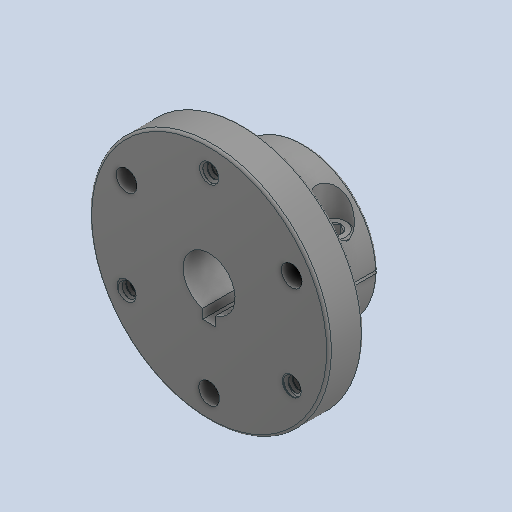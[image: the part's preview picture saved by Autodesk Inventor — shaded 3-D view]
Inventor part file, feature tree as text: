
AUTODESK INVENTOR PART (.ipt)
format: ipt  version: 2022 (Build 260153000, 153)  size: 1,361,408 bytes
history: native  units: in
note: dims shown in document units (in); Inventor stores cm internally (conversion verified against a paired STEP export)
features: other x2, mirror x1
ambient origin geometry x8: Origin, YZ Plane, XZ Plane, XY Plane, X Axis, Y Axis, Z Axis, Center Point
bodies: Solid1 (feature_tree), Solid2 (feature_tree), Solid3 (feature_tree)
feature tree (3):
  mirror  "MIRROR2"
  other  "CUT-SWEEP2"
  other  "BOSS-EXTRUDE1"
